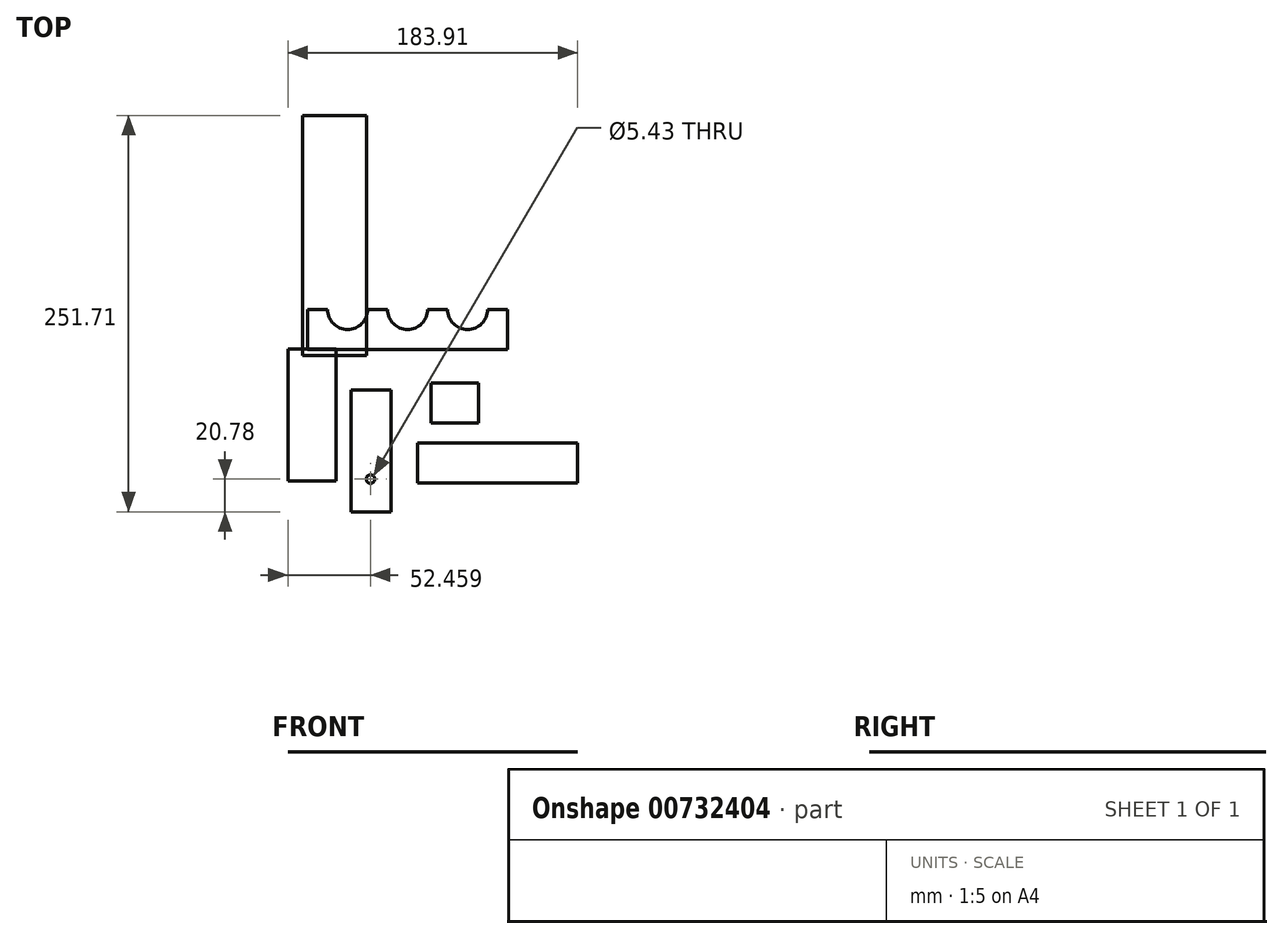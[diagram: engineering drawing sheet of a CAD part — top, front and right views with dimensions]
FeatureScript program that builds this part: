
annotation { "Feature Type Name" : "Feature", "Feature Type Description" : "" }
export const myFeature = defineFeature(function(context is Context, id is Id, definition is map)
    precondition{}
    {
        {
            var Q0;
            Q0=qCreatedBy(makeId("Top.planeOp"),FACE);
            var sketch = newSketch(context, id + "F0", { "sketchPlane" : qUnion([Q0])});
            skLineSegment(sketch, "E0.bottom", {"start": v(-64.77, 39.53) * mm, "end": v(-52.07, 39.53) * mm});
            skLineSegment(sketch, "E0.top", {"start": v(-64.77, 14.13) * mm, "end": v(62.23, 14.13) * mm});
            skLineSegment(sketch, "E0.left", {"start": v(-64.77, 39.53) * mm, "end": v(-64.77, 14.13) * mm});
            skLineSegment(sketch, "E0.right", {"start": v(62.23, 39.53) * mm, "end": v(62.23, 14.13) * mm});
            skArc(sketch, "E1", {"start": v(-52.07, 39.53) * mm, "mid": v(-39.37, 26.83) * mm, "end": v(-26.67, 39.53) * mm});
            skArc(sketch, "E2", {"start": v(-13.97, 39.53) * mm, "mid": v(-1.27, 26.83) * mm, "end": v(11.43, 39.53) * mm});
            skArc(sketch, "E3", {"start": v(24.13, 39.53) * mm, "mid": v(36.83, 26.83) * mm, "end": v(49.53, 39.53) * mm});
            skLineSegment(sketch, "E4.trimOffspring", {"start": v(49.53, 39.53) * mm, "end": v(62.23, 39.53) * mm});
            skLineSegment(sketch, "E5.trimOffspring", {"start": v(11.43, 39.53) * mm, "end": v(24.13, 39.53) * mm});
            skLineSegment(sketch, "E6.trimOffspring", {"start": v(-26.67, 39.53) * mm, "end": v(-13.97, 39.53) * mm});
            skSolve(sketch);
        }
        {
            var Q0;
            Q0 = qSketchRegion(id + "F0", true);
            extrude(context, id + "F1", {"entities" : qUnion([Q0]), "depth" : 1 / 203.2 * mm, "offsetDistance" : 25.4 * mm});
        }
        {
            var Q0;
            Q0=qCreatedBy(makeId("Top.planeOp"),FACE);
            var sketch = newSketch(context, id + "F2", { "sketchPlane" : qUnion([Q0])});
            skLineSegment(sketch, "E7.bottom", {"start": v(-77.27, 14.48) * mm, "end": v(-46.79, 14.48) * mm});
            skLineSegment(sketch, "E7.top", {"start": v(-77.27, -69.34) * mm, "end": v(-46.79, -69.34) * mm});
            skLineSegment(sketch, "E7.left", {"start": v(-77.27, 14.48) * mm, "end": v(-77.27, -69.34) * mm});
            skLineSegment(sketch, "E7.right", {"start": v(-46.79, 14.48) * mm, "end": v(-46.79, -69.34) * mm});
            skSolve(sketch);
        }
        {
            var Q0;
            Q0 = qSketchRegion(id + "F2", true);
            extrude(context, id + "F3", {"entities" : qUnion([Q0]), "depth" : 1 / 203.2 * mm, "offsetDistance" : 25.4 * mm});
        }
        {
            var Q0;
            Q0=qCreatedBy(makeId("Top.planeOp"),FACE);
            var sketch = newSketch(context, id + "F4", { "sketchPlane" : qUnion([Q0])});
            skLineSegment(sketch, "E8.bottom", {"start": v(-37.23, -11.48) * mm, "end": v(-11.83, -11.48) * mm});
            skLineSegment(sketch, "E8.top", {"start": v(-37.23, -88.95) * mm, "end": v(-11.83, -88.95) * mm});
            skLineSegment(sketch, "E8.left", {"start": v(-37.23, -11.48) * mm, "end": v(-37.23, -88.95) * mm});
            skLineSegment(sketch, "E8.right", {"start": v(-11.83, -11.48) * mm, "end": v(-11.83, -88.95) * mm});
            skCircle(sketch, "E9", {"center": v(-24.81, -68.17) * mm, "radius": 2.72 * mm});
            skSolve(sketch);
        }
        {
            var Q0;
            Q0 = qSketchRegion(id + "F4", true);
            extrude(context, id + "F5", {"entities" : qUnion([Q0]), "depth" : 1 / 203.2 * mm, "offsetDistance" : 25.4 * mm});
        }
        {
            var Q0;
            Q0=qCreatedBy(makeId("Top.planeOp"),FACE);
            var sketch = newSketch(context, id + "F6", { "sketchPlane" : qUnion([Q0])});
            skLineSegment(sketch, "E10.bottom", {"start": v(13.47, -7.1) * mm, "end": v(43.95, -7.1) * mm});
            skLineSegment(sketch, "E10.top", {"start": v(13.47, -32.5) * mm, "end": v(43.95, -32.5) * mm});
            skLineSegment(sketch, "E10.left", {"start": v(13.47, -7.1) * mm, "end": v(13.47, -32.5) * mm});
            skLineSegment(sketch, "E10.right", {"start": v(43.95, -7.1) * mm, "end": v(43.95, -32.5) * mm});
            skSolve(sketch);
        }
        {
            var Q0;
            Q0 = qSketchRegion(id + "F6", true);
            extrude(context, id + "F7", {"entities" : qUnion([Q0]), "depth" : 1 / 203.2 * mm, "offsetDistance" : 25.4 * mm});
        }
        {
            var Q0;
            Q0=qCreatedBy(makeId("Top.planeOp"),FACE);
            var sketch = newSketch(context, id + "F8", { "sketchPlane" : qUnion([Q0])});
            skLineSegment(sketch, "E11.bottom", {"start": v(5.04, -45.28) * mm, "end": v(106.64, -45.28) * mm});
            skLineSegment(sketch, "E11.top", {"start": v(5.04, -70.68) * mm, "end": v(106.64, -70.68) * mm});
            skLineSegment(sketch, "E11.left", {"start": v(5.04, -45.28) * mm, "end": v(5.04, -70.68) * mm});
            skLineSegment(sketch, "E11.right", {"start": v(106.64, -45.28) * mm, "end": v(106.64, -70.68) * mm});
            skSolve(sketch);
        }
        {
            var Q0;
            Q0 = qSketchRegion(id + "F8", true);
            extrude(context, id + "F9", {"entities" : qUnion([Q0]), "depth" : 1 / 203.2 * mm, "offsetDistance" : 25.4 * mm});
        }
        {
            var Q0;
            Q0=qCreatedBy(makeId("Top.planeOp"),FACE);
            var sketch = newSketch(context, id + "F10", { "sketchPlane" : qUnion([Q0])});
            skLineSegment(sketch, "E12.bottom", {"start": v(-27.18, 10.36) * mm, "end": v(-67.82, 10.36) * mm});
            skLineSegment(sketch, "E12.top", {"start": v(-27.18, 162.76) * mm, "end": v(-67.82, 162.76) * mm});
            skLineSegment(sketch, "E12.left", {"start": v(-27.18, 10.36) * mm, "end": v(-27.18, 162.76) * mm});
            skLineSegment(sketch, "E12.right", {"start": v(-67.82, 10.36) * mm, "end": v(-67.82, 162.76) * mm});
            skSolve(sketch);
        }
        {
            var Q0;
            Q0 = qSketchRegion(id + "F10", true);
            extrude(context, id + "F11", {"entities" : qUnion([Q0]), "depth" : 1 / 203.2 * mm, "offsetDistance" : 25.4 * mm});
        }
    });
